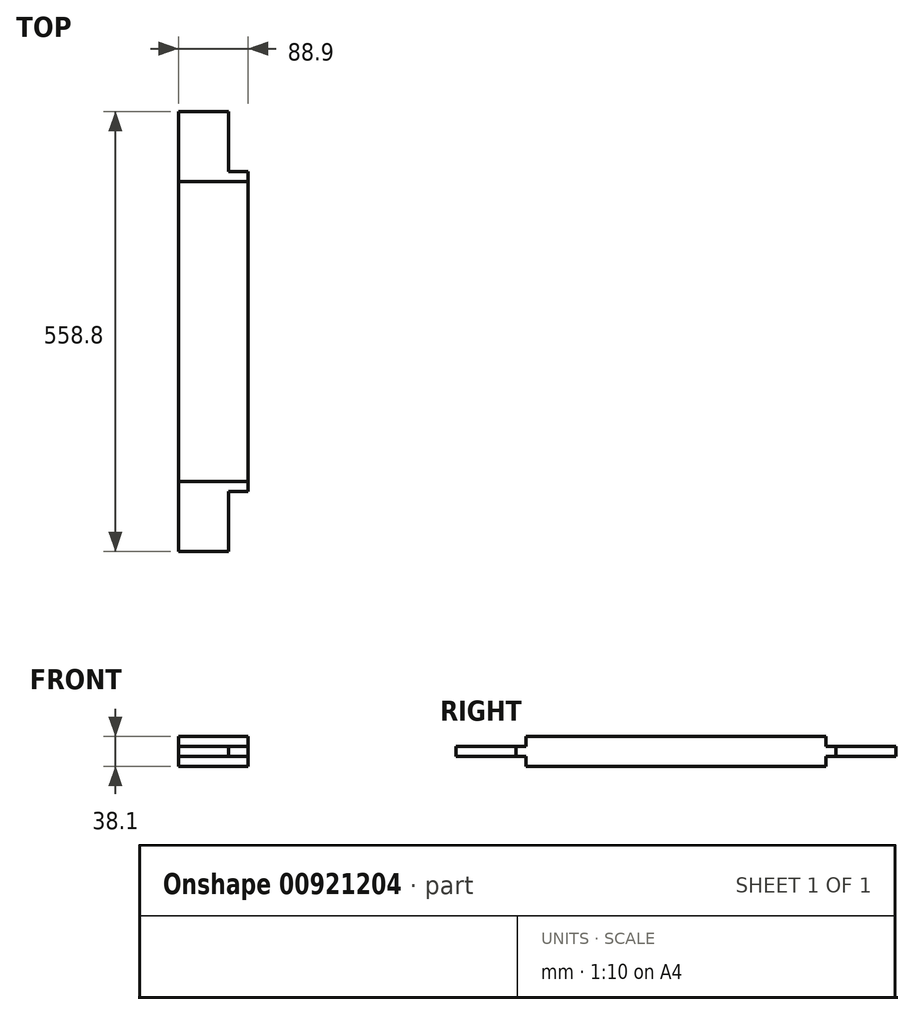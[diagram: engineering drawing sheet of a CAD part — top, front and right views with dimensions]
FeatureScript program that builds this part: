
annotation { "Feature Type Name" : "Feature", "Feature Type Description" : "" }
export const myFeature = defineFeature(function(context is Context, id is Id, definition is map)
    precondition{}
    {
        {
            var Q0;
            Q0=qCreatedBy(makeId("Front.planeOp"),FACE);
            var sketch = newSketch(context, id + "F0", { "sketchPlane" : qUnion([Q0])});
            skLineSegment(sketch, "E0.bottom", {"start": v(0, 0) * mm, "end": v(88.9, 0) * mm});
            skLineSegment(sketch, "E0.top", {"start": v(0, 38.1) * mm, "end": v(88.9, 38.1) * mm});
            skLineSegment(sketch, "E0.left", {"start": v(0, 0) * mm, "end": v(0, 38.1) * mm});
            skLineSegment(sketch, "E0.right", {"start": v(88.9, 0) * mm, "end": v(88.9, 38.1) * mm});
            skSolve(sketch);
        }
        {
            var Q0;
            Q0 = qSketchRegion(id + "F0", true);
            extrude(context, id + "F1", {"entities" : qUnion([Q0]), "depth" : 190.5 * mm, "offsetDistance" : 25.4 * mm});
        }
        {
            var Q0;
            Q0=makeQuery(id+"F1.opExtrude","CAP_FACE",FACE,{"disambiguationData":[OSD([sQuery(id+"F0.wireOp",EDGE,"E0.bottom"),sQuery(id+"F0.wireOp",EDGE,"E0.top"),sQuery(id+"F0.wireOp",EDGE,"E0.left"),sQuery(id+"F0.wireOp",EDGE,"E0.right")])],"isStart":false});
            var sketch = newSketch(context, id + "F2", { "sketchPlane" : qUnion([Q0])});
            skLineSegment(sketch, "E1", {"start": v(88.9, 19.05) * mm, "end": v(0, 19.05) * mm, "construction": true});
            skLineSegment(sketch, "E2.bottom", {"start": v(88.9, 25.4) * mm, "end": v(0, 25.4) * mm});
            skLineSegment(sketch, "E2.top", {"start": v(88.9, 12.7) * mm, "end": v(0, 12.7) * mm});
            skLineSegment(sketch, "E2.left", {"start": v(88.9, 25.4) * mm, "end": v(88.9, 12.7) * mm});
            skLineSegment(sketch, "E2.right", {"start": v(0, 25.4) * mm, "end": v(0, 12.7) * mm});
            skSolve(sketch);
        }
        {
            var Q0;
            Q0 = qSketchRegion(id + "F2", true);
            extrude(context, id + "F3", {"entities" : qUnion([Q0]), "operationType" : NewBodyOperationType.ADD, "depth" : 12.7 * mm, "offsetDistance" : 25.4 * mm});
        }
        {
            var Q0;
            Q0=makeQuery(id+"F3.opExtrude","CAP_FACE",FACE,{"disambiguationData":[OSD([sQuery(id+"F2.wireOp",EDGE,"E2.bottom"),sQuery(id+"F2.wireOp",EDGE,"E2.top"),sQuery(id+"F2.wireOp",EDGE,"E2.left"),sQuery(id+"F2.wireOp",EDGE,"E2.right")])],"isStart":false});
            var sketch = newSketch(context, id + "F4", { "sketchPlane" : qUnion([Q0])});
            skLineSegment(sketch, "E3.bottom", {"start": v(0, 25.4) * mm, "end": v(63.5, 25.4) * mm});
            skLineSegment(sketch, "E3.top", {"start": v(0, 12.7) * mm, "end": v(63.5, 12.7) * mm});
            skLineSegment(sketch, "E3.left", {"start": v(0, 25.4) * mm, "end": v(0, 12.7) * mm});
            skLineSegment(sketch, "E3.right", {"start": v(63.5, 25.4) * mm, "end": v(63.5, 12.7) * mm});
            skSolve(sketch);
        }
        {
            var Q0;
            Q0 = qSketchRegion(id + "F4", true);
            extrude(context, id + "F5", {"entities" : qUnion([Q0]), "operationType" : NewBodyOperationType.ADD, "depth" : 76.2 * mm, "offsetDistance" : 25.4 * mm});
        }
        {
            var Q0;
            Q0=makeQuery(id+"F1.opExtrude","SWEPT_BODY",BODY,{"disambiguationData":[OSD([sQuery(id+"F0.wireOp",EDGE,"E0.bottom"),sQuery(id+"F0.wireOp",EDGE,"E0.top"),sQuery(id+"F0.wireOp",EDGE,"E0.left"),sQuery(id+"F0.wireOp",EDGE,"E0.right")])]});
            var Q1;
            Q1=makeQuery(id+"F1.opExtrude","CAP_FACE",FACE,{"disambiguationData":[OSD([sQuery(id+"F0.wireOp",EDGE,"E0.bottom"),sQuery(id+"F0.wireOp",EDGE,"E0.top"),sQuery(id+"F0.wireOp",EDGE,"E0.left"),sQuery(id+"F0.wireOp",EDGE,"E0.right")])],"isStart":true});
            mirror(context, id + "F6", {"operationType" : NewBodyOperationType.ADD, "entities" : qUnion([Q0]), "mirrorPlane" : qUnion([Q1])});
        }
    });
